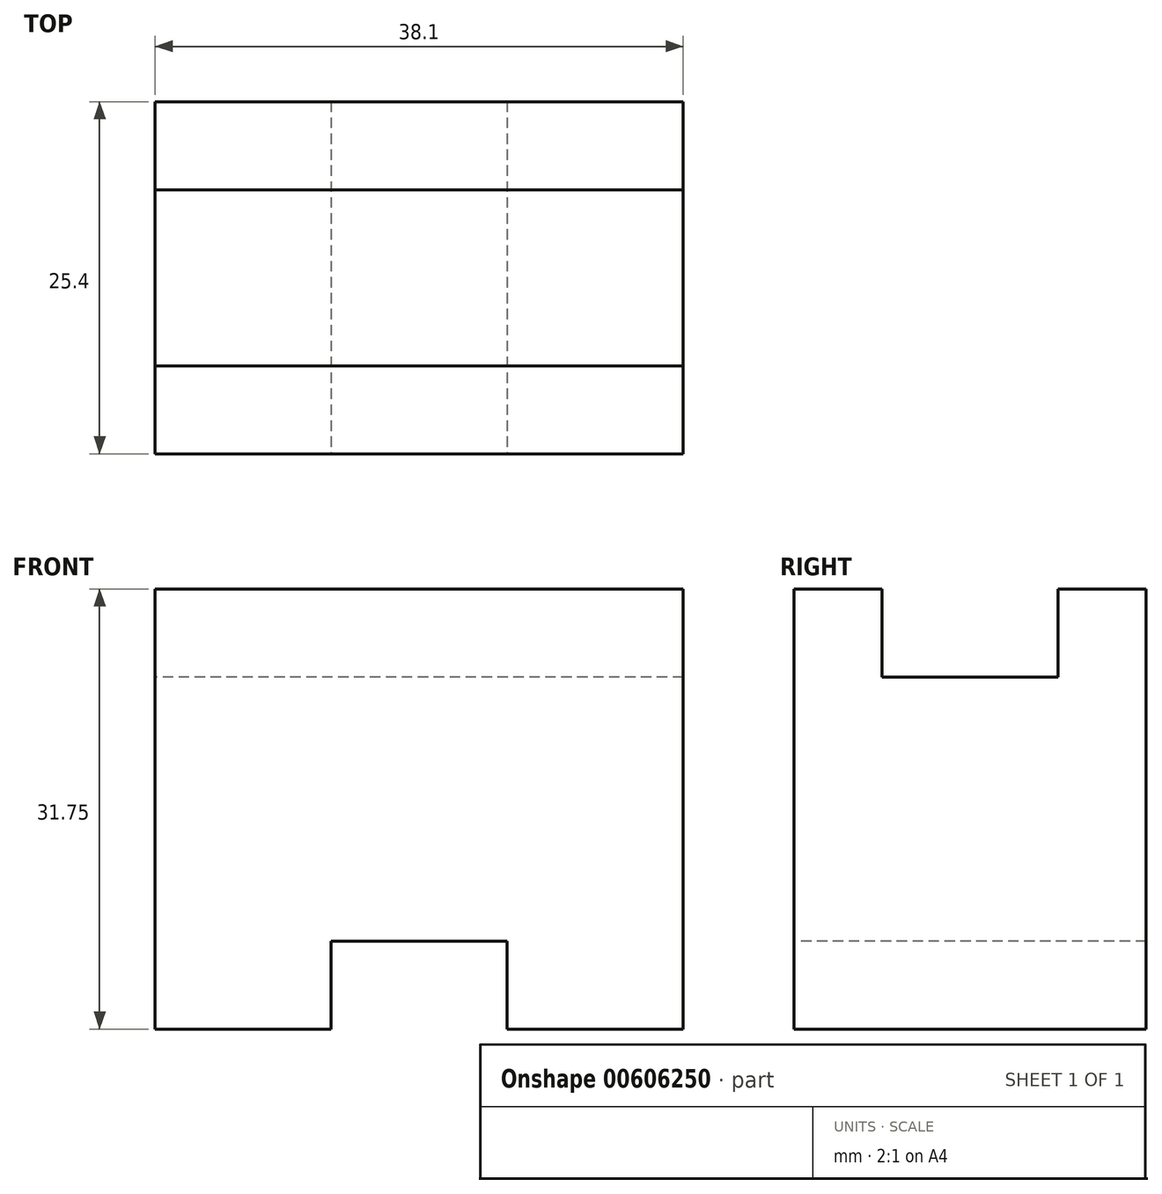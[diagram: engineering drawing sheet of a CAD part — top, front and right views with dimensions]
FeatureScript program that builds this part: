
annotation { "Feature Type Name" : "Feature", "Feature Type Description" : "" }
export const myFeature = defineFeature(function(context is Context, id is Id, definition is map)
    precondition{}
    {
        {
            var Q0;
            Q0=qCreatedBy(makeId("Right.planeOp"),FACE);
            var sketch = newSketch(context, id + "F0", { "sketchPlane" : qUnion([Q0])});
            skLineSegment(sketch, "E0", {"start": v(0, 0) * mm, "end": v(25.4, 0) * mm});
            skLineSegment(sketch, "E1", {"start": v(0, 0) * mm, "end": v(0, 31.75) * mm});
            skLineSegment(sketch, "E2", {"start": v(0, 31.75) * mm, "end": v(6.35, 31.75) * mm});
            skLineSegment(sketch, "E3", {"start": v(25.4, 0) * mm, "end": v(25.4, 31.75) * mm});
            skLineSegment(sketch, "E4", {"start": v(25.4, 31.75) * mm, "end": v(19.05, 31.75) * mm});
            skLineSegment(sketch, "E5", {"start": v(6.35, 31.75) * mm, "end": v(6.35, 25.4) * mm});
            skLineSegment(sketch, "E6", {"start": v(19.05, 31.75) * mm, "end": v(19.05, 25.4) * mm});
            skLineSegment(sketch, "E7", {"start": v(6.35, 25.4) * mm, "end": v(19.05, 25.4) * mm});
            skSolve(sketch);
        }
        {
            var Q0;
            Q0=makeQuery(id+"F0.imprint","IMPRINT",FACE,{"disambiguationData":[TD([[makeQuery(id+"F0.imprint","IMPRINT",EDGE,{"derivedFrom":sQuery(id+"F0.wireOp",EDGE,"E0")}),1.0]])]});
            extrude(context, id + "F1", {"entities" : qUnion([Q0]), "depth" : 38.1 * mm, "offsetDistance" : 25.4 * mm});
        }
        {
            var Q0;
            Q0=makeQuery(id+"F1.opExtrude","SWEPT_FACE",FACE,{"disambiguationData":[OSD([sQuery(id+"F0.wireOp",EDGE,"E1")])]});
            var sketch = newSketch(context, id + "F2", { "sketchPlane" : qUnion([Q0])});
            skLineSegment(sketch, "E8", {"start": v(0, 0) * mm, "end": v(12.7, 0) * mm});
            skLineSegment(sketch, "E9", {"start": v(12.7, 0) * mm, "end": v(12.7, 6.35) * mm});
            skLineSegment(sketch, "E10", {"start": v(12.7, 6.35) * mm, "end": v(25.4, 6.35) * mm});
            skLineSegment(sketch, "E11", {"start": v(25.4, 6.35) * mm, "end": v(25.4, 0) * mm});
            skSolve(sketch);
        }
        {
            var Q0;
            {var subQ0=sQuery(id+"F2.wireOp",EDGE,"E9");Q0=makeQuery(id+"F2.imprint","IMPRINT",FACE,{"disambiguationData":[TD([[makeQuery(id+"F2.imprint","IMPRINT",EDGE,{"derivedFrom":subQ0}),-1.0]])]});}
            extrude(context, id + "F3", {"entities" : qUnion([Q0]), "operationType" : NewBodyOperationType.REMOVE, "oppositeDirection" : true, "depth" : 25.4 * mm, "offsetDistance" : 25.4 * mm});
        }
    });
